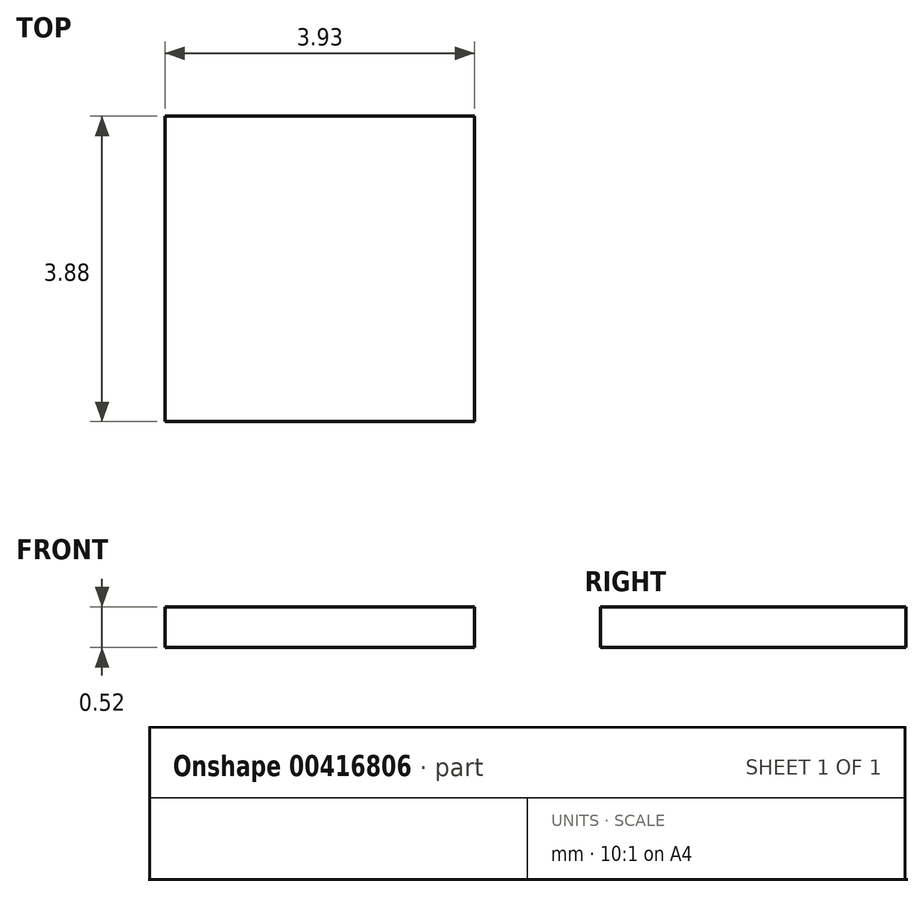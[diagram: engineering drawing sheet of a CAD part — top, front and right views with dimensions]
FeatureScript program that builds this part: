
annotation { "Feature Type Name" : "Feature", "Feature Type Description" : "" }
export const myFeature = defineFeature(function(context is Context, id is Id, definition is map)
    precondition{}
    {
        {
            var Q0;
            Q0=qCreatedBy(makeId("Top.planeOp"),FACE);
            var sketch = newSketch(context, id + "F0", { "sketchPlane" : qUnion([Q0])});
            skLineSegment(sketch, "E0.bottom", {"start": v(0, 0) * mm, "end": v(3.93, 0) * mm});
            skLineSegment(sketch, "E0.top", {"start": v(0, 3.88) * mm, "end": v(3.93, 3.88) * mm});
            skLineSegment(sketch, "E0.left", {"start": v(0, 0) * mm, "end": v(0, 3.88) * mm});
            skLineSegment(sketch, "E0.right", {"start": v(3.93, 0) * mm, "end": v(3.93, 3.88) * mm});
            skSolve(sketch);
        }
        {
            var Q0;
            Q0 = qSketchRegion(id + "F0", true);
            extrude(context, id + "F1", {"entities" : qUnion([Q0]), "depth" : .52 * mm, "offsetDistance" : 25.4 * mm});
        }
    });
